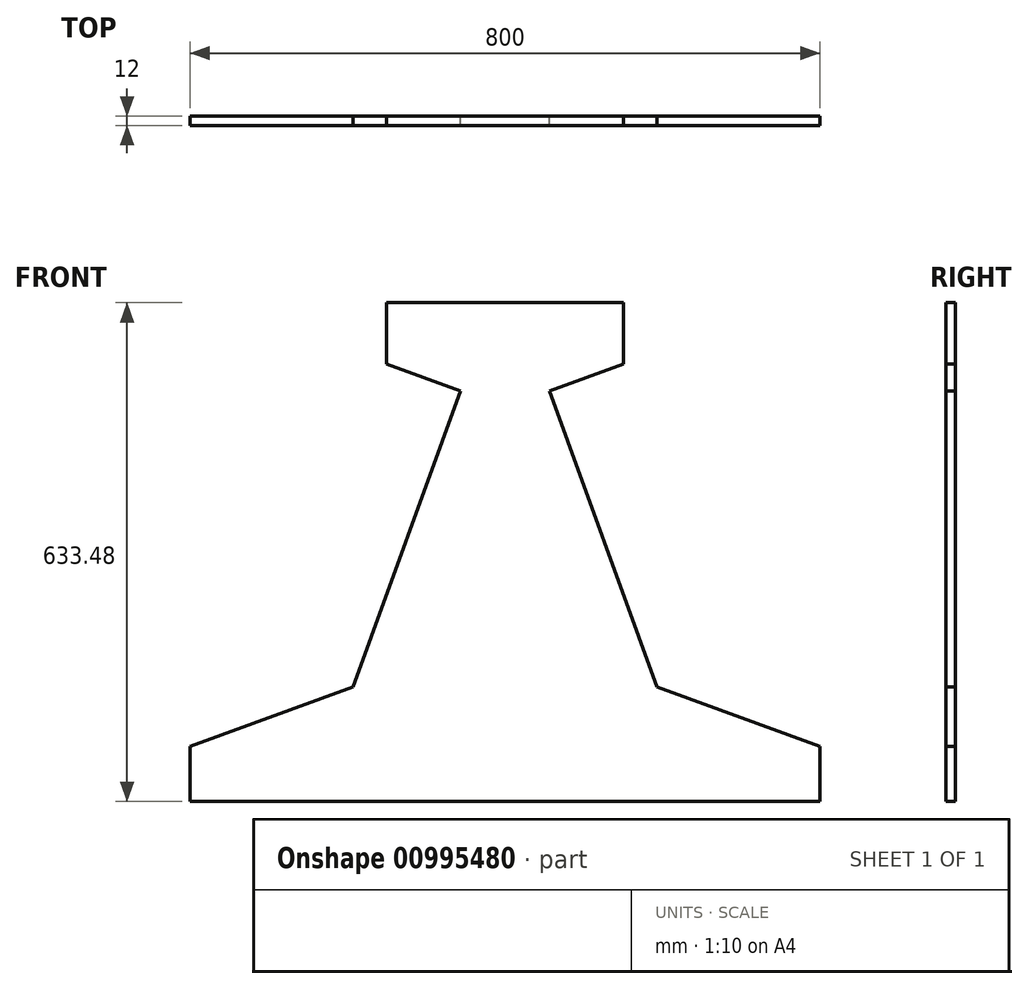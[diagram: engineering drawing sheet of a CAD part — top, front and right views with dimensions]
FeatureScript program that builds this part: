
annotation { "Feature Type Name" : "Feature", "Feature Type Description" : "" }
export const myFeature = defineFeature(function(context is Context, id is Id, definition is map)
    precondition{}
    {
        {
            var Q0;
            Q0=qCreatedBy(makeId("Front.planeOp"),FACE);
            var sketch = newSketch(context, id + "F0", { "sketchPlane" : qUnion([Q0])});
            skLineSegment(sketch, "E0.top", {"start": v(-223.42, -214.71) * mm, "end": v(576.58, -214.71) * mm});
            skLineSegment(sketch, "E1", {"start": v(-223.42, -144.71) * mm, "end": v(-16.7, -69.47) * mm});
            skLineSegment(sketch, "E2", {"start": v(369.84, -69.47) * mm, "end": v(576.58, -144.71) * mm});
            skLineSegment(sketch, "E3", {"start": v(-16.7, -69.47) * mm, "end": v(120.12, 306.4) * mm});
            skLineSegment(sketch, "E4", {"start": v(120.12, 306.4) * mm, "end": v(26.15, 340.6) * mm});
            skLineSegment(sketch, "E5", {"start": v(26.15, 340.6) * mm, "end": v(26.15, 418.77) * mm});
            skLineSegment(sketch, "E6", {"start": v(26.15, 418.77) * mm, "end": v(327, 418.77) * mm});
            skLineSegment(sketch, "E7", {"start": v(327, 418.77) * mm, "end": v(327, 340.6) * mm});
            skLineSegment(sketch, "E8", {"start": v(327, 340.6) * mm, "end": v(233.04, 306.4) * mm});
            skLineSegment(sketch, "E9", {"start": v(233.04, 306.4) * mm, "end": v(369.84, -69.47) * mm});
            skLineSegment(sketch, "E10", {"start": v(576.58, -214.71) * mm, "end": v(576.58, -144.71) * mm});
            skLineSegment(sketch, "E11", {"start": v(-223.42, -214.71) * mm, "end": v(-223.42, -144.71) * mm});
            skSolve(sketch);
        }
        {
            var Q0;
            Q0=qSketchRegion(id+"F0",true);
            extrude(context, id + "F1", {"entities" : qUnion([Q0]), "depth" : 12 * mm, "offsetDistance" : 25.4 * mm});
        }
    });
